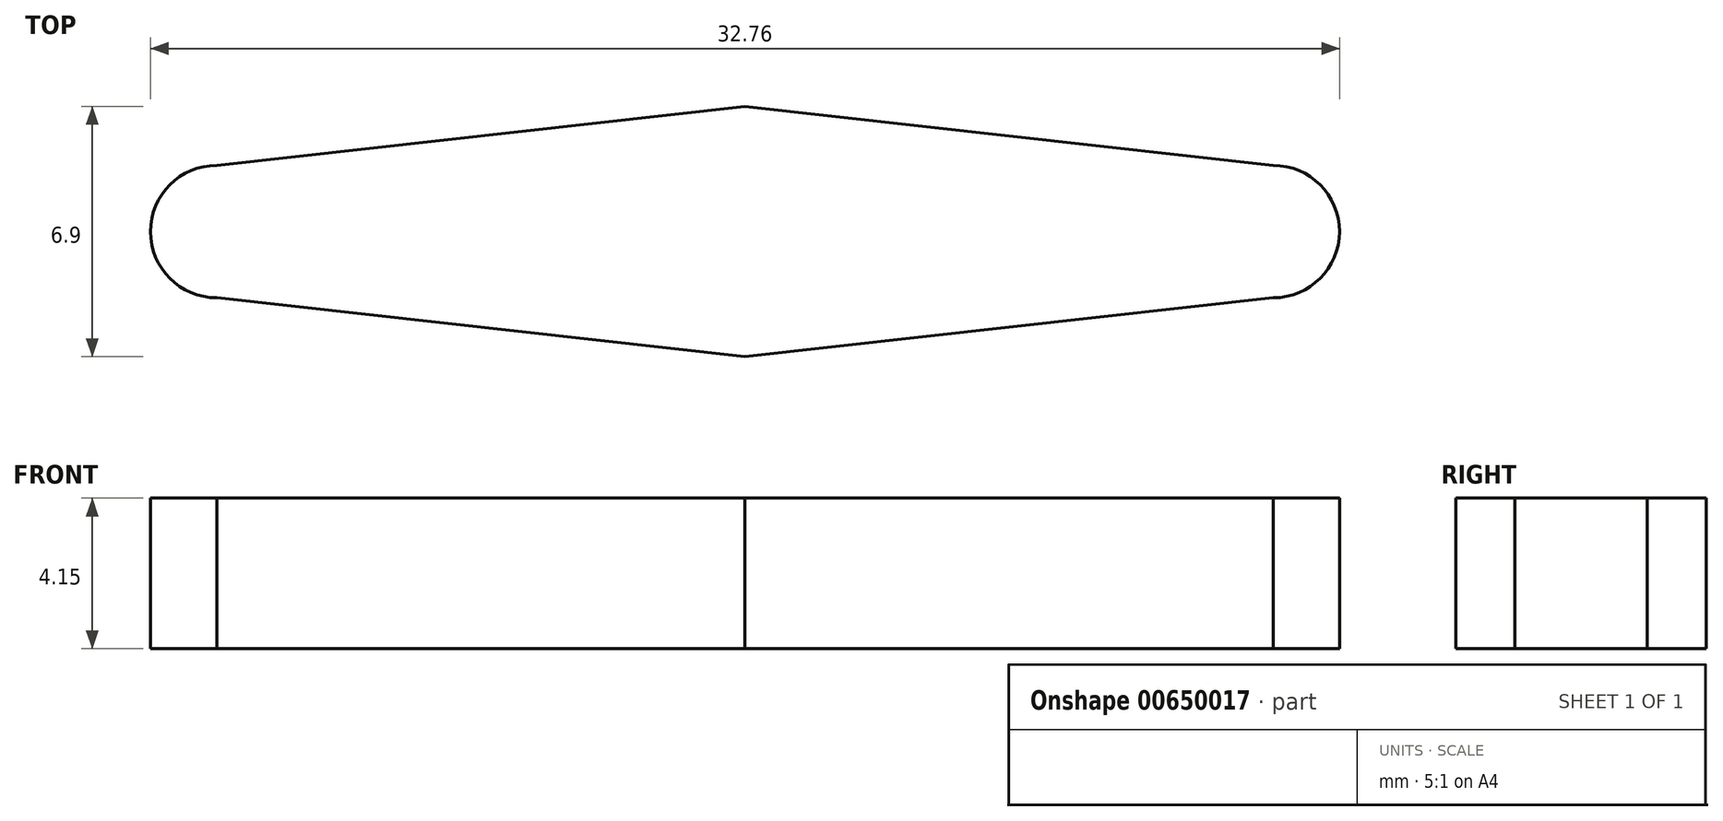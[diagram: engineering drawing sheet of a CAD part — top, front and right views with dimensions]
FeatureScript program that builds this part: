
annotation { "Feature Type Name" : "Feature", "Feature Type Description" : "" }
export const myFeature = defineFeature(function(context is Context, id is Id, definition is map)
    precondition{}
    {
        {
            assignVariable(context, id + "F0", {"name" : "horn_thickness", "anyValue" : 4.15});
        }
        {
            var Q0;
            Q0=qCreatedBy(makeId("Top.planeOp"),FACE);
            var sketch = newSketch(context, id + "F1", { "sketchPlane" : qUnion([Q0])});
            skCircle(sketch, "E0", {"center": v(0, 0) * mm, "radius": 3.45 * mm});
            skLineSegment(sketch, "E1", {"start": v(0, 0) * mm, "end": v(-16.38, 0) * mm, "construction": true});
            skLineSegment(sketch, "E2", {"start": v(0, 0) * mm, "end": v(16.38, 0) * mm, "construction": true});
            skLineSegment(sketch, "E3", {"start": v(-16.38, 0) * mm, "end": v(-14.55, 0) * mm, "construction": true});
            skLineSegment(sketch, "E4", {"start": v(16.38, 0) * mm, "end": v(14.55, 0) * mm, "construction": true});
            skCircle(sketch, "E5", {"center": v(-14.55, 0) * mm, "radius": 1.83 * mm});
            skCircle(sketch, "E6", {"center": v(14.55, 0) * mm, "radius": 1.83 * mm});
            skLineSegment(sketch, "E7", {"start": v(0, 0) * mm, "end": v(0, 3.45) * mm, "construction": true});
            skLineSegment(sketch, "E8", {"start": v(0, 0) * mm, "end": v(0, -3.45) * mm, "construction": true});
            skLineSegment(sketch, "E9", {"start": v(-14.55, 0) * mm, "end": v(-14.55, 1.83) * mm, "construction": true});
            skLineSegment(sketch, "E10", {"start": v(-14.55, 0) * mm, "end": v(-14.55, -1.83) * mm, "construction": true});
            skLineSegment(sketch, "E11", {"start": v(14.55, 0) * mm, "end": v(14.55, 1.83) * mm, "construction": true});
            skLineSegment(sketch, "E12", {"start": v(14.55, 0) * mm, "end": v(14.55, -1.83) * mm, "construction": true});
            skLineSegment(sketch, "E13", {"start": v(-14.55, 1.82) * mm, "end": v(0, 3.45) * mm});
            skLineSegment(sketch, "E14", {"start": v(14.55, 1.82) * mm, "end": v(0, 3.45) * mm});
            skLineSegment(sketch, "E15", {"start": v(14.55, -1.82) * mm, "end": v(0, -3.45) * mm});
            skLineSegment(sketch, "E16", {"start": v(0, -3.45) * mm, "end": v(-14.55, -1.82) * mm});
            skSolve(sketch);
        }
        {
            var Q0;
            {var subQ0=sQuery(id+"F1.wireOp",EDGE,"E13");var subQ1=sQuery(id+"F1.wireOp",EDGE,"E0");var subQ2=makeQuery(id+"F1.imprint","INTERSECT",VERTEX,{"derivedFrom":[subQ1,subQ0]});Q0=makeQuery(id+"F1.imprint","IMPRINT",FACE,{"disambiguationData":[TD([[makeQuery(id+"F1.imprint","IMPRINT",EDGE,{"disambiguationData":[TD([[subQ2,-1.0]])],"derivedFrom":subQ1}),-1.0]])]});}
            var Q1;
            {var subQ0=sQuery(id+"F1.wireOp",EDGE,"E5");var subQ1=makeQuery(id+"F1.imprint","INTERSECT",VERTEX,{"derivedFrom":[subQ0,sQuery(id+"F1.wireOp",EDGE,"E13")]});Q1=makeQuery(id+"F1.imprint","IMPRINT",FACE,{"disambiguationData":[TD([[makeQuery(id+"F1.imprint","IMPRINT",EDGE,{"disambiguationData":[TD([[subQ1,-1.0]])],"derivedFrom":subQ0}),1.0]])]});}
            var Q2;
            {var subQ1=sQuery(id+"F1.wireOp",EDGE,"E13");var subQ2=sQuery(id+"F1.wireOp",EDGE,"E0");var subQ5=makeQuery(id+"F1.imprint","INTERSECT",VERTEX,{"derivedFrom":[subQ2,subQ1]});Q2=makeQuery(id+"F1.imprint","IMPRINT",FACE,{"disambiguationData":[TD([[makeQuery(id+"F1.imprint","IMPRINT",EDGE,{"disambiguationData":[TD([[subQ5,-1.0]])],"derivedFrom":subQ2}),1.0]])]});}
            var Q3;
            {var subQ0=sQuery(id+"F1.wireOp",EDGE,"E14");var subQ1=sQuery(id+"F1.wireOp",EDGE,"E0");var subQ2=makeQuery(id+"F1.imprint","INTERSECT",VERTEX,{"derivedFrom":[subQ1,subQ0]});Q3=makeQuery(id+"F1.imprint","IMPRINT",FACE,{"disambiguationData":[TD([[makeQuery(id+"F1.imprint","IMPRINT",EDGE,{"disambiguationData":[TD([[subQ2,1.0]])],"derivedFrom":subQ1}),-1.0]])]});}
            var Q4;
            {var subQ0=sQuery(id+"F1.wireOp",EDGE,"E6");var subQ1=makeQuery(id+"F1.imprint","INTERSECT",VERTEX,{"derivedFrom":[subQ0,sQuery(id+"F1.wireOp",EDGE,"E14")]});Q4=makeQuery(id+"F1.imprint","IMPRINT",FACE,{"disambiguationData":[TD([[makeQuery(id+"F1.imprint","IMPRINT",EDGE,{"disambiguationData":[TD([[subQ1,-1.0]])],"derivedFrom":subQ0}),1.0]])]});}
            extrude(context, id + "F2", {"entities" : qUnion([Q0, Q1, Q2, Q3, Q4]), "depth" : (getVariable(context, 'horn_thickness')) * mm, "offsetDistance" : 25 * mm});
        }
    });
